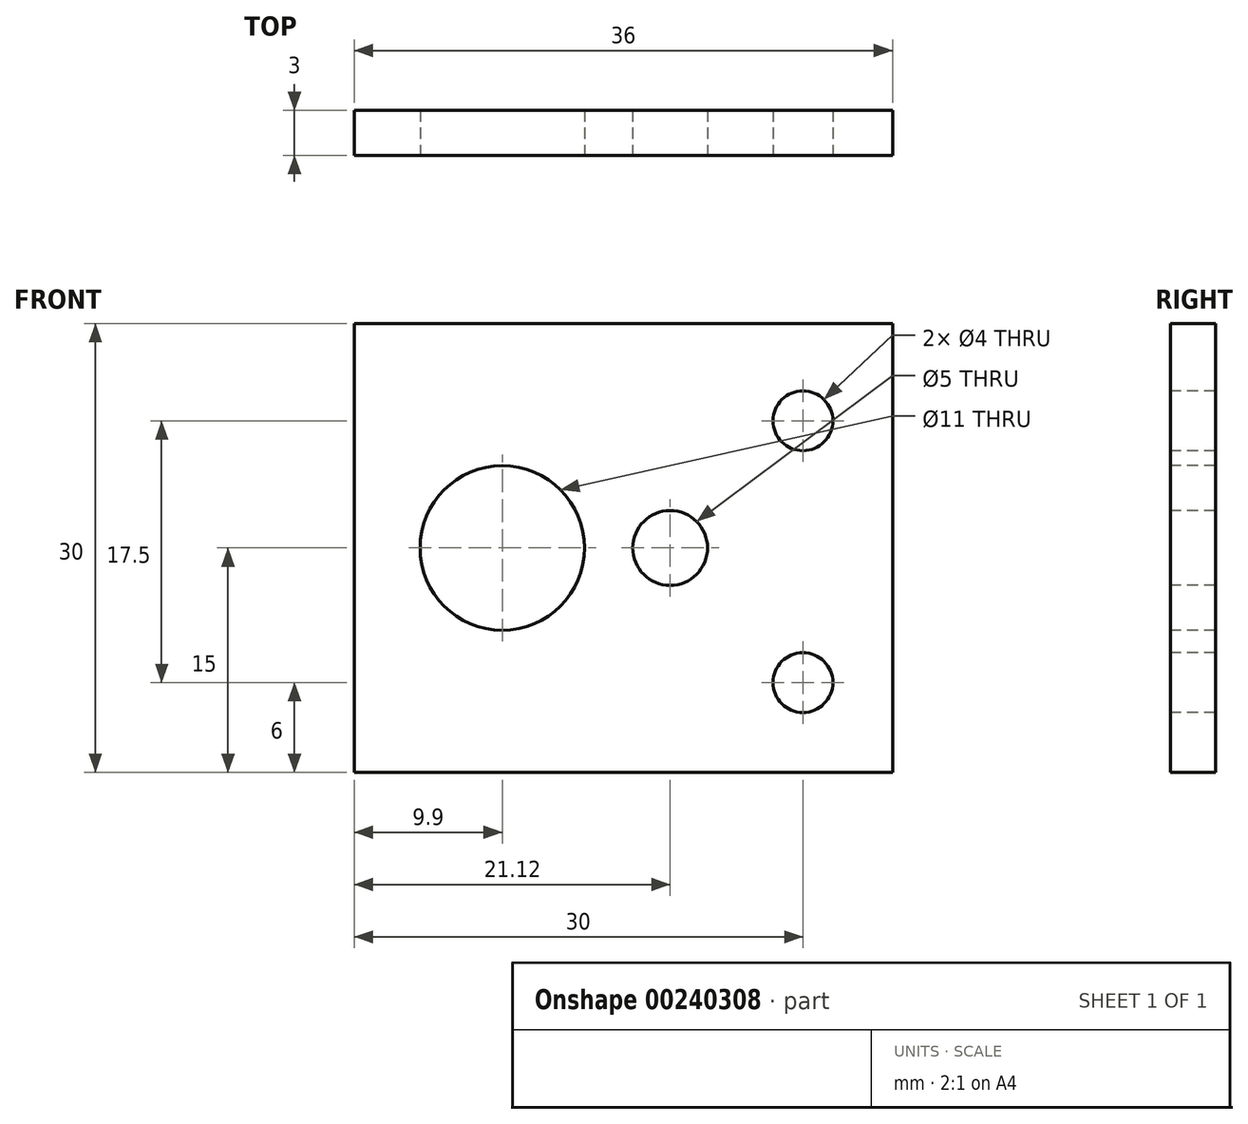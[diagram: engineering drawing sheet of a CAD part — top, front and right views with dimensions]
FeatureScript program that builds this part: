
annotation { "Feature Type Name" : "Feature", "Feature Type Description" : "" }
export const myFeature = defineFeature(function(context is Context, id is Id, definition is map)
    precondition{}
    {
        {
            var Q0;
            Q0=qCreatedBy(makeId("Top.planeOp"),FACE);
            var sketch = newSketch(context, id + "F0", { "sketchPlane" : qUnion([Q0])});
            skLineSegment(sketch, "E0.bottom", {"start": v(-30, 0) * mm, "end": v(6, 0) * mm});
            skLineSegment(sketch, "E0.top", {"start": v(-30, -3) * mm, "end": v(6, -3) * mm});
            skLineSegment(sketch, "E0.left", {"start": v(-30, 0) * mm, "end": v(-30, -3) * mm});
            skLineSegment(sketch, "E0.right", {"start": v(6, 0) * mm, "end": v(6, -3) * mm});
            skSolve(sketch);
        }
        {
            var Q0;
            Q0=qSketchRegion(id+"F0",true);
            extrude(context, id + "F1", {"entities" : qUnion([Q0]), "depth" : 3 * mm});
        }
        {
            var Q0;
            Q0=makeQuery(id+"F1.opExtrude","SWEPT_FACE",FACE,{"disambiguationData":[OSD([sQuery(id+"F0.wireOp",EDGE,"E0.top")])]});
            var sketch = newSketch(context, id + "F2", { "sketchPlane" : qUnion([Q0])});
            skLineSegment(sketch, "E1.bottom", {"start": v(-30, 0) * mm, "end": v(6, 0) * mm});
            skLineSegment(sketch, "E1.top", {"start": v(-30, 30) * mm, "end": v(6, 30) * mm});
            skLineSegment(sketch, "E1.left", {"start": v(-30, 0) * mm, "end": v(-30, 30) * mm});
            skLineSegment(sketch, "E1.right", {"start": v(6, 0) * mm, "end": v(6, 30) * mm});
            skCircle(sketch, "E2", {"center": v(0, 23.5) * mm, "radius": 2 * mm});
            skCircle(sketch, "E3", {"center": v(0, 6) * mm, "radius": 2 * mm});
            skPoint(sketch, "E4", {"position": v(-8.88, 15) * mm});
            skLineSegment(sketch, "E5", {"start": v(-20.1, 15) * mm, "end": v(-8.88, 15) * mm, "construction": true});
            skCircle(sketch, "E6", {"center": v(-8.88, 15) * mm, "radius": 2.5 * mm});
            skPoint(sketch, "E7", {"position": v(-20.1, 15) * mm});
            skCircle(sketch, "E8", {"center": v(-20.1, 15) * mm, "radius": 5.5 * mm});
            skSolve(sketch);
        }
        {
            var Q0;
            Q0=qSketchRegion(id+"F2",true);
            extrude(context, id + "F3", {"entities" : qUnion([Q0]), "operationType" : NewBodyOperationType.ADD, "oppositeDirection" : true, "depth" : 3 * mm});
        }
    });
